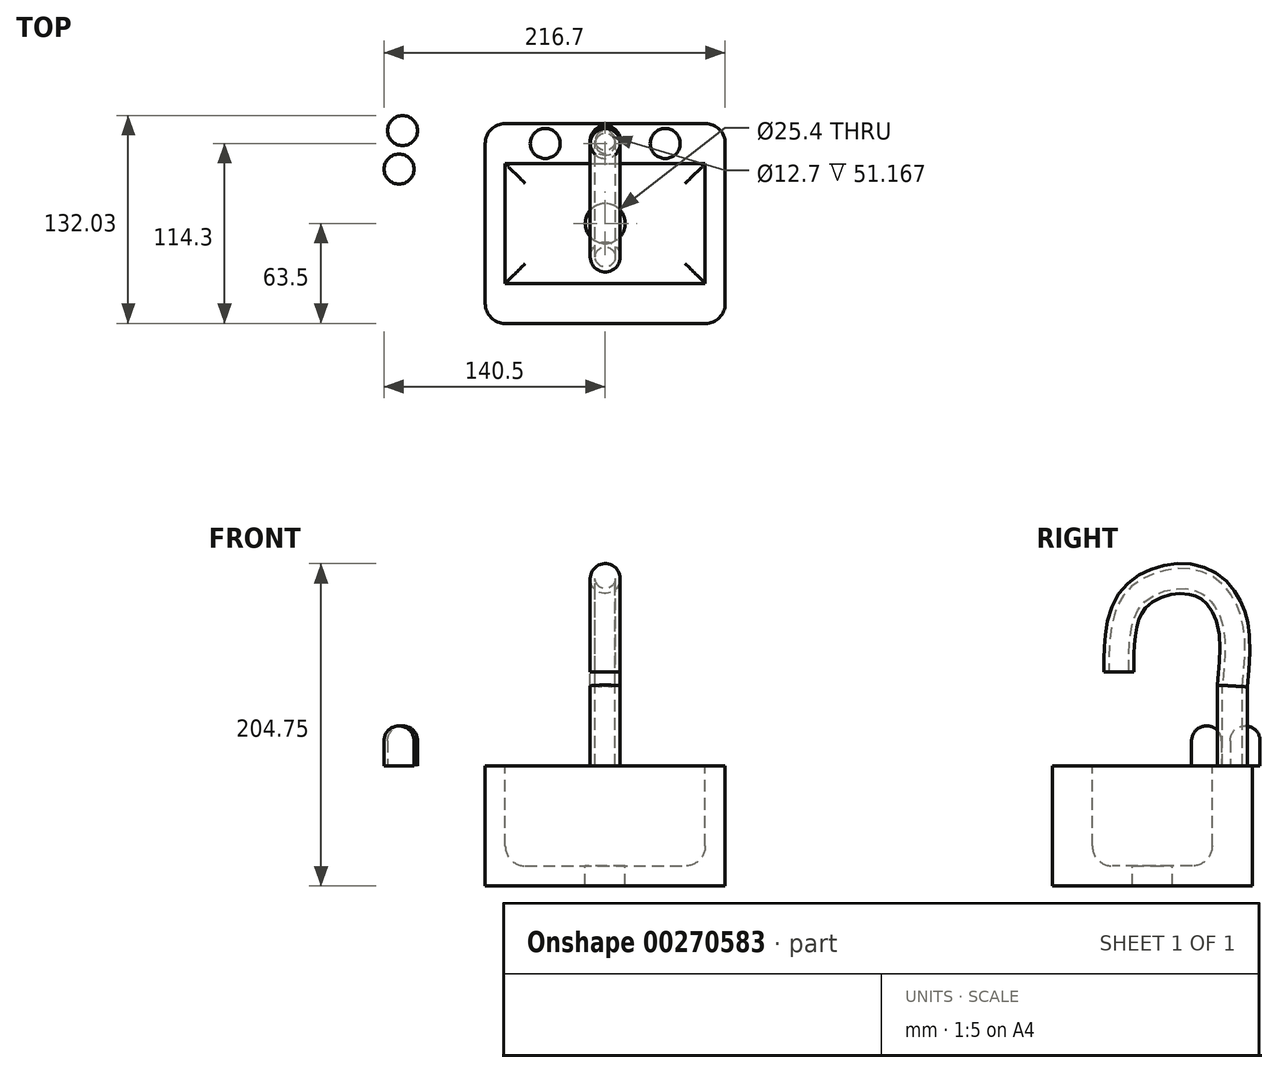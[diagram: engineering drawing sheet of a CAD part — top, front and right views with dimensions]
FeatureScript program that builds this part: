
annotation { "Feature Type Name" : "Feature", "Feature Type Description" : "" }
export const myFeature = defineFeature(function(context is Context, id is Id, definition is map)
    precondition{}
    {
        {
            var Q0;
            Q0=qCreatedBy(makeId("Top.planeOp"),FACE);
            var sketch = newSketch(context, id + "F0", { "sketchPlane" : qUnion([Q0])});
            skLineSegment(sketch, "E0.bottom", {"start": v(-76.2, 63.5) * mm, "end": v(76.2, 63.5) * mm});
            skLineSegment(sketch, "E0.top", {"start": v(-76.2, -63.5) * mm, "end": v(76.2, -63.5) * mm});
            skLineSegment(sketch, "E0.left", {"start": v(-76.2, 63.5) * mm, "end": v(-76.2, -63.5) * mm});
            skLineSegment(sketch, "E0.right", {"start": v(76.2, 63.5) * mm, "end": v(76.2, -63.5) * mm});
            skPoint(sketch, "E0.middle", {"position": v(0, 0) * mm});
            skLineSegment(sketch, "E1.bottom", {"start": v(-63.5, 38.1) * mm, "end": v(63.5, 38.1) * mm});
            skLineSegment(sketch, "E1.top", {"start": v(-63.5, -38.1) * mm, "end": v(63.5, -38.1) * mm});
            skLineSegment(sketch, "E1.left", {"start": v(-63.5, 38.1) * mm, "end": v(-63.5, -38.1) * mm});
            skLineSegment(sketch, "E1.right", {"start": v(63.5, 38.1) * mm, "end": v(63.5, -38.1) * mm});
            skLineSegment(sketch, "E2", {"start": v(0, 0) * mm, "end": v(0, 50.8) * mm});
            skPoint(sketch, "E2.endSnap0", {"position": v(0, 38.1) * mm});
            skCircle(sketch, "E3", {"center": v(0, 50.8) * mm, "radius": 9.53 * mm});
            skCircle(sketch, "E4", {"center": v(0, 50.8) * mm, "radius": 6.35 * mm});
            skCircle(sketch, "E5", {"center": v(0, 0) * mm, "radius": 12.7 * mm});
            skCircle(sketch, "E6", {"center": v(-128.72, 59) * mm, "radius": 9.53 * mm});
            skCircle(sketch, "E7", {"center": v(-130.97, 34.55) * mm, "radius": 9.53 * mm});
            skLineSegment(sketch, "E8", {"start": v(0, 50.8) * mm, "end": v(-38.1, 50.8) * mm});
            skLineSegment(sketch, "E9", {"start": v(-38.1, 50.8) * mm, "end": v(38.1, 50.8) * mm});
            skCircle(sketch, "E10", {"center": v(-38.1, 50.8) * mm, "radius": 9.53 * mm});
            skCircle(sketch, "E11", {"center": v(38.1, 50.8) * mm, "radius": 9.53 * mm});
            skSolve(sketch);
        }
        {
            var Q0;
            Q0=makeQuery(id+"F0.imprint","IMPRINT",FACE,{"disambiguationData":[TD([[makeQuery(id+"F0.imprint","IMPRINT",EDGE,{"derivedFrom":sQuery(id+"F0.wireOp",EDGE,"E0.bottom")}),-1.0]])]});
            var Q1;
            Q1=makeQuery(id+"F0.imprint","IMPRINT",FACE,{"disambiguationData":[TD([[makeQuery(id+"F0.imprint","IMPRINT",EDGE,{"derivedFrom":sQuery(id+"F0.wireOp",EDGE,"E1.top")}),1.0]])]});
            var Q2;
            Q2=makeQuery(id+"F0.imprint","IMPRINT",FACE,{"disambiguationData":[TD([[makeQuery(id+"F0.imprint","IMPRINT",EDGE,{"derivedFrom":sQuery(id+"F0.wireOp",EDGE,"E4")}),1.0]])]});
            var Q3;
            Q3=makeQuery(id+"F0.imprint","IMPRINT",FACE,{"disambiguationData":[TD([[makeQuery(id+"F0.imprint","IMPRINT",EDGE,{"derivedFrom":sQuery(id+"F0.wireOp",EDGE,"E3")}),1.0]])]});
            var Q4;
            Q4=makeQuery(id+"F0.imprint","IMPRINT",FACE,{"disambiguationData":[TD([[makeQuery(id+"F0.imprint","IMPRINT",EDGE,{"derivedFrom":sQuery(id+"F0.wireOp",EDGE,"E10")}),1.0]])]});
            var Q5;
            Q5=makeQuery(id+"F0.imprint","IMPRINT",FACE,{"disambiguationData":[TD([[makeQuery(id+"F0.imprint","IMPRINT",EDGE,{"derivedFrom":sQuery(id+"F0.wireOp",EDGE,"E11")}),1.0]])]});
            extrude(context, id + "F1", {"entities" : qUnion([Q0, Q1, Q2, Q3, Q4, Q5]), "oppositeDirection" : true, "depth" : 76.2 * mm});
        }
        {
            var Q0;
            Q0=makeQuery(id+"F0.imprint","IMPRINT",FACE,{"disambiguationData":[TD([[makeQuery(id+"F0.imprint","IMPRINT",EDGE,{"derivedFrom":sQuery(id+"F0.wireOp",EDGE,"E1.top")}),1.0]])]});
            extrude(context, id + "F2", {"entities" : qUnion([Q0]), "operationType" : NewBodyOperationType.REMOVE, "oppositeDirection" : true, "depth" : 63.5 * mm});
        }
        {
            var Q0;
            Q0=qCreatedBy(makeId("Right.planeOp"),FACE);
            var sketch = newSketch(context, id + "F3", { "sketchPlane" : qUnion([Q0])});
            skLineSegment(sketch, "E12", {"start": v(0, 0) * mm, "end": v(50.8, 0) * mm});
            skLineSegment(sketch, "E13", {"start": v(50.8, 0) * mm, "end": v(50.8, 50.8) * mm});
            skLineSegment(sketch, "E14", {"start": v(0, 0) * mm, "end": v(25.4, 0) * mm});
            skFitSpline(sketch, "E15", {"points": [v(50.8, 50.8) * mm, v(50.8, 91.37) * mm, v(29.57, 117.36) * mm, v(-10.8, 107.3) * mm, v(-21.27, 59.8) * mm], "startDerivative": vector(19.4, 167.79) * mm, "endDerivative": vector(-1.05, -200.58) * mm});
            skSolve(sketch);
        }
        {
            var Q0;
            Q0=makeQuery(id+"F0.imprint","IMPRINT",FACE,{"disambiguationData":[TD([[makeQuery(id+"F0.imprint","IMPRINT",EDGE,{"derivedFrom":sQuery(id+"F0.wireOp",EDGE,"E3")}),1.0]])]});
            var Q1;
            Q1=sQuery(id+"F3.wireOp",EDGE,"E13");
            var Q2;
            Q2=sQuery(id+"F3.wireOp",EDGE,"796fb245-dab0-48ba-b3a3-2da9f5135e8c");
            var Q3;
            Q3=sQuery(id+"F3.wireOp",EDGE,"E15");
            sweep(context, id + "F4", {"operationType" : NewBodyOperationType.ADD, "profiles" : qUnion([Q0]), "path" : qUnion([Q1, Q2, Q3])});
        }
        {
            var Q0;
            Q0=makeQuery(id+"F0.imprint","IMPRINT",FACE,{"disambiguationData":[TD([[makeQuery(id+"F0.imprint","IMPRINT",EDGE,{"derivedFrom":sQuery(id+"F0.wireOp",EDGE,"E6")}),1.0]])]});
            var Q1;
            Q1=makeQuery(id+"F0.imprint","IMPRINT",FACE,{"disambiguationData":[TD([[makeQuery(id+"F0.imprint","IMPRINT",EDGE,{"derivedFrom":sQuery(id+"F0.wireOp",EDGE,"E7")}),1.0]])]});
            extrude(context, id + "F5", {"entities" : qUnion([Q0, Q1]), "depth" : 25.4 * mm});
        }
        {
            var Q0;
            Q0=makeQuery(id+"F5.opExtrude","CAP_EDGE",EDGE,{"disambiguationData":[OSD([sQuery(id+"F0.wireOp",EDGE,"E7")])],"isStart":false});
            var Q1;
            Q1=makeQuery(id+"F5.opExtrude","CAP_EDGE",EDGE,{"disambiguationData":[OSD([sQuery(id+"F0.wireOp",EDGE,"E6")])],"isStart":false});
            fillet(context, id + "F6", {"entities" : qUnion([Q0, Q1]), "radius" : 9.4 * mm, "tangentPropagation" : true, "allowEdgeOverflow" : false});
        }
        {
            var Q0;
            Q0=makeQuery(id+"F0.imprint","IMPRINT",FACE,{"disambiguationData":[TD([[makeQuery(id+"F0.imprint","IMPRINT",EDGE,{"derivedFrom":sQuery(id+"F0.wireOp",EDGE,"E10")}),1.0]])]});
            var Q1;
            Q1=makeQuery(id+"F0.imprint","IMPRINT",FACE,{"disambiguationData":[TD([[makeQuery(id+"F0.imprint","IMPRINT",EDGE,{"derivedFrom":sQuery(id+"F0.wireOp",EDGE,"E11")}),1.0]])]});
            extrude(context, id + "F7", {"entities" : qUnion([Q0, Q1]), "operationType" : NewBodyOperationType.ADD, "depth" : 0.03 * mm});
        }
        {
            var Q0;
            Q0=makeQuery(id+"F2.boolean.opBoolean","COPY",EDGE,{"derivedFrom":makeQuery(id+"F2.opExtrude","CAP_EDGE",EDGE,{"disambiguationData":[OSD([sQuery(id+"F0.wireOp",EDGE,"E1.left")])],"isStart":false})});
            var Q1;
            Q1=makeQuery(id+"F2.boolean.opBoolean","COPY",EDGE,{"derivedFrom":makeQuery(id+"F2.opExtrude","CAP_EDGE",EDGE,{"disambiguationData":[OSD([sQuery(id+"F0.wireOp",EDGE,"E1.bottom")])],"isStart":false})});
            var Q2;
            Q2=makeQuery(id+"F2.boolean.opBoolean","COPY",EDGE,{"derivedFrom":makeQuery(id+"F2.opExtrude","CAP_EDGE",EDGE,{"disambiguationData":[OSD([sQuery(id+"F0.wireOp",EDGE,"E1.right")])],"isStart":false})});
            var Q3;
            Q3=makeQuery(id+"F2.boolean.opBoolean","COPY",EDGE,{"derivedFrom":makeQuery(id+"F2.opExtrude","CAP_EDGE",EDGE,{"disambiguationData":[OSD([sQuery(id+"F0.wireOp",EDGE,"E1.top")])],"isStart":false})});
            var Q4;
            Q4=makeQuery(id+"F2.boolean.opBoolean","COPY",EDGE,{"derivedFrom":makeQuery(id+"F2.opExtrude","CAP_EDGE",EDGE,{"disambiguationData":[OSD([sQuery(id+"F0.wireOp",EDGE,"E5")])],"isStart":false})});
            var Q5;
            Q5=makeQuery(id+"F1.opExtrude","SWEPT_EDGE",EDGE,{"disambiguationData":[OSD([sQuery(id+"F0.wireOp",EDGE,"E0.top"),sQuery(id+"F0.wireOp",EDGE,"E0.left")])]});
            var Q6;
            Q6=makeQuery(id+"F1.opExtrude","SWEPT_EDGE",EDGE,{"disambiguationData":[OSD([sQuery(id+"F0.wireOp",EDGE,"E0.bottom"),sQuery(id+"F0.wireOp",EDGE,"E0.left")])]});
            var Q7;
            Q7=makeQuery(id+"F1.opExtrude","SWEPT_EDGE",EDGE,{"disambiguationData":[OSD([sQuery(id+"F0.wireOp",EDGE,"E0.bottom"),sQuery(id+"F0.wireOp",EDGE,"E0.right")])]});
            var Q8;
            Q8=makeQuery(id+"F1.opExtrude","SWEPT_EDGE",EDGE,{"disambiguationData":[OSD([sQuery(id+"F0.wireOp",EDGE,"E0.top"),sQuery(id+"F0.wireOp",EDGE,"E0.right")])]});
            fillet(context, id + "F8", {"entities" : qUnion([Q0, Q1, Q2, Q3, Q4, Q5, Q6, Q7, Q8]), "radius" : 12.7 * mm, "tangentPropagation" : true, "allowEdgeOverflow" : false});
        }
    });
